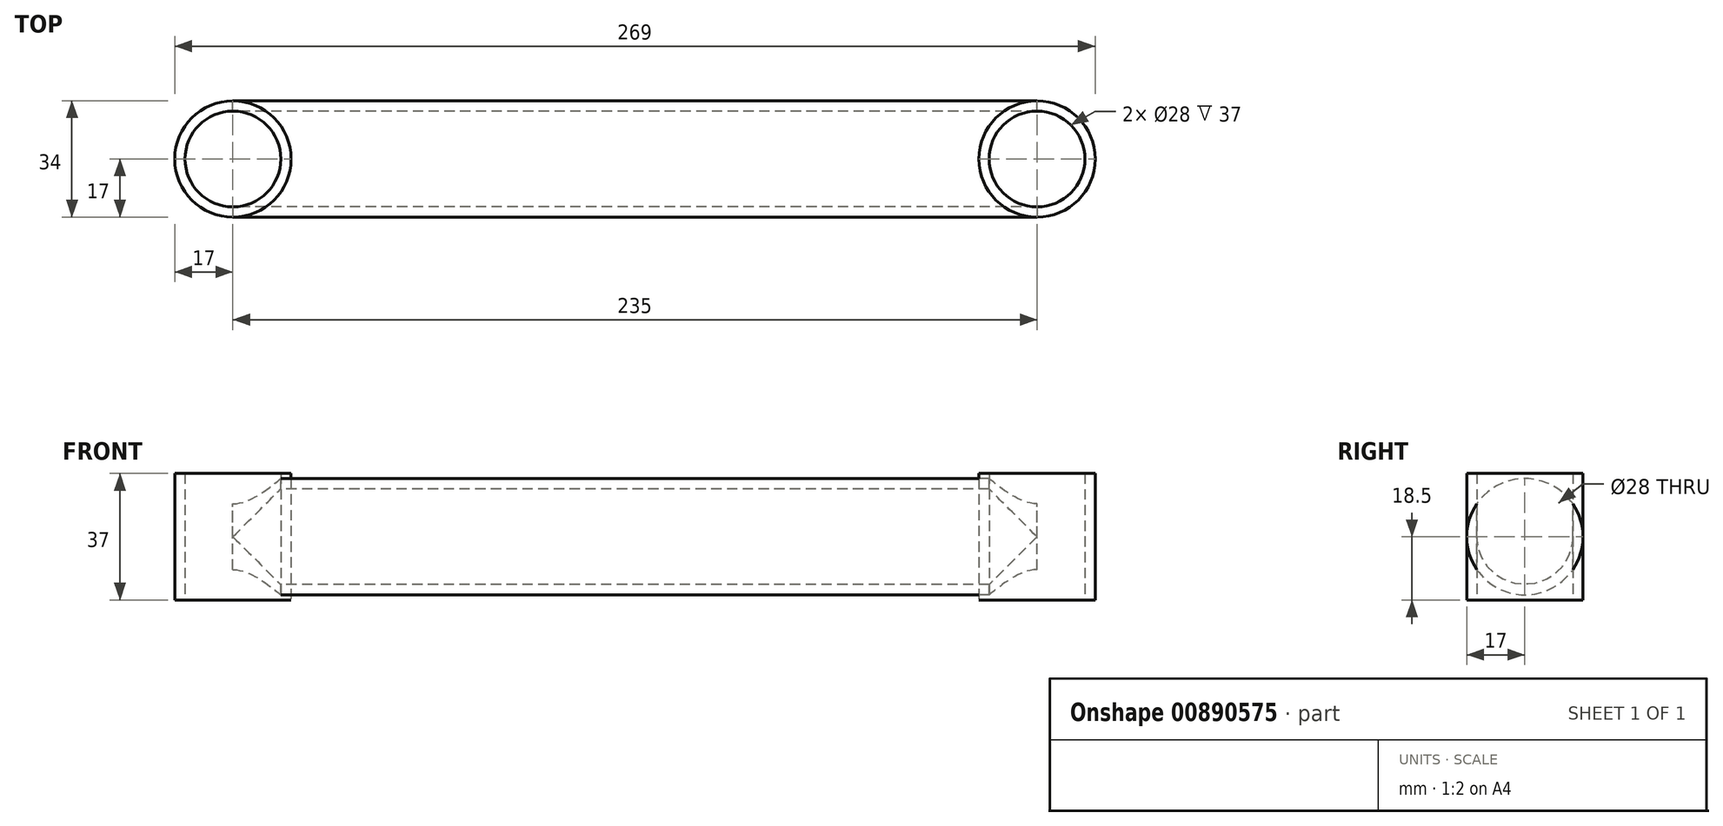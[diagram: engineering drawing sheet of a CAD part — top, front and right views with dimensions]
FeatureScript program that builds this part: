
annotation { "Feature Type Name" : "Feature", "Feature Type Description" : "" }
export const myFeature = defineFeature(function(context is Context, id is Id, definition is map)
    precondition{}
    {
        {
            var Q0;
            Q0=qCreatedBy(makeId("Top.planeOp"),FACE);
            var sketch = newSketch(context, id + "F0", { "sketchPlane" : qUnion([Q0])});
            skLineSegment(sketch, "E0", {"start": v(-117.5, 0) * mm, "end": v(117.5, 0) * mm});
            skCircle(sketch, "E1", {"center": v(-117.5, 0) * mm, "radius": 17 * mm});
            skCircle(sketch, "E2", {"center": v(117.5, 0) * mm, "radius": 17 * mm});
            skCircle(sketch, "E3", {"center": v(-117.5, 0) * mm, "radius": 14 * mm});
            skCircle(sketch, "E4", {"center": v(117.5, 0) * mm, "radius": 14 * mm});
            skSolve(sketch);
        }
        {
            var Q0;
            Q0 = qSketchRegion(id + "F0", true);
            extrude(context, id + "F1", {"entities" : qUnion([Q0]), "depth" : 18.5 * mm, "offsetDistance" : 25 * mm, "hasSecondDirection" : true, "secondDirectionOppositeDirection" : true, "secondDirectionDepth" : 18.5 * mm});
        }
        {
            var Q0;
            Q0=sQuery(id+"F0.wireOp",EDGE,"E0");
            cPlane(context, id + "F2", {"entities" : qUnion([Q0]), "cplaneType" : CPlaneType.MID_PLANE, "offset" : 25 * mm, "width" : 150 * mm, "height" : 150 * mm});
        }
        {
            var Q0;
            Q0=qCreatedBy(id+"F2.planeOp",FACE);
            var sketch = newSketch(context, id + "F3", { "sketchPlane" : qUnion([Q0])});
            skCircle(sketch, "E5", {"center": v(0, 0) * mm, "radius": 17 * mm});
            skCircle(sketch, "E6", {"center": v(0, 0) * mm, "radius": 14 * mm});
            skSolve(sketch);
        }
        {
            var Q0;
            Q0 = qSketchRegion(id + "F3", true);
            extrude(context, id + "F4", {"entities" : qUnion([Q0]), "depth" : 117.5 * mm, "offsetDistance" : 25 * mm, "hasSecondDirection" : true, "secondDirectionOppositeDirection" : true, "secondDirectionDepth" : 117.5 * mm});
        }
        {
            var Q0;
            Q0=makeQuery(id+"F1.opExtrude","CAP_FACE",FACE,{"disambiguationData":[OSD([sQuery(id+"F0.wireOp",EDGE,"E1"),sQuery(id+"F0.wireOp",EDGE,"E3")])],"isStart":false});
            var sketch = newSketch(context, id + "F5", { "sketchPlane" : qUnion([Q0])});
            skCircle(sketch, "E7", {"center": v(-117.5, 0) * mm, "radius": 14 * mm});
            skCircle(sketch, "E8", {"center": v(117.5, 0) * mm, "radius": 14 * mm});
            skSolve(sketch);
        }
        {
            var Q0;
            Q0 = qSketchRegion(id + "F5", true);
            extrude(context, id + "F6", {"entities" : qUnion([Q0]), "operationType" : NewBodyOperationType.REMOVE, "oppositeDirection" : true, "depth" : 60 * mm, "offsetDistance" : 25 * mm});
        }
    });
